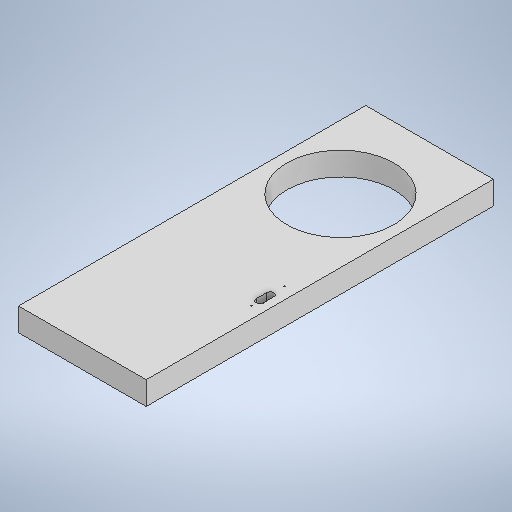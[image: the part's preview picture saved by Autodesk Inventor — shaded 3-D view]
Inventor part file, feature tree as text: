
AUTODESK INVENTOR PART (.ipt)
format: ipt  version: 2025.1 (Build 291241000, 241)  size: 363,520 bytes
history: native  units: mm
features: extrude x3, sketch x3
ambient origin geometry x8: Origin, YZ Plane, XZ Plane, XY Plane, X Axis, Y Axis, Z Axis, Center Point
bodies: Solid1 (feature_tree)
feature tree (6):
  extrude  "Extrusion1"  Depth=1947.0mm
  extrude  "Extrusion2"  Depth=130.0mm
  extrude  "Extrusion3"  Depth=10.0mm TaperAngle=0.0deg
  sketch  "Sketch6"  dims[d0=716.0mm d1=1947.0mm]
  sketch  "Sketch7"  dims[d2=130.0mm d3=0.0mm d4=600.0mm]
  sketch  "Sketch9"  dims[d5=500.0mm d6=80.0mm d7=0.0mm d8=40.0mm d9=681.0mm d10=100.0mm d12=7.0mm d13=60.0mm d14=7.0mm d15=187.0mm d16=10.0mm d17=0.0mm d18=65.0mm]
